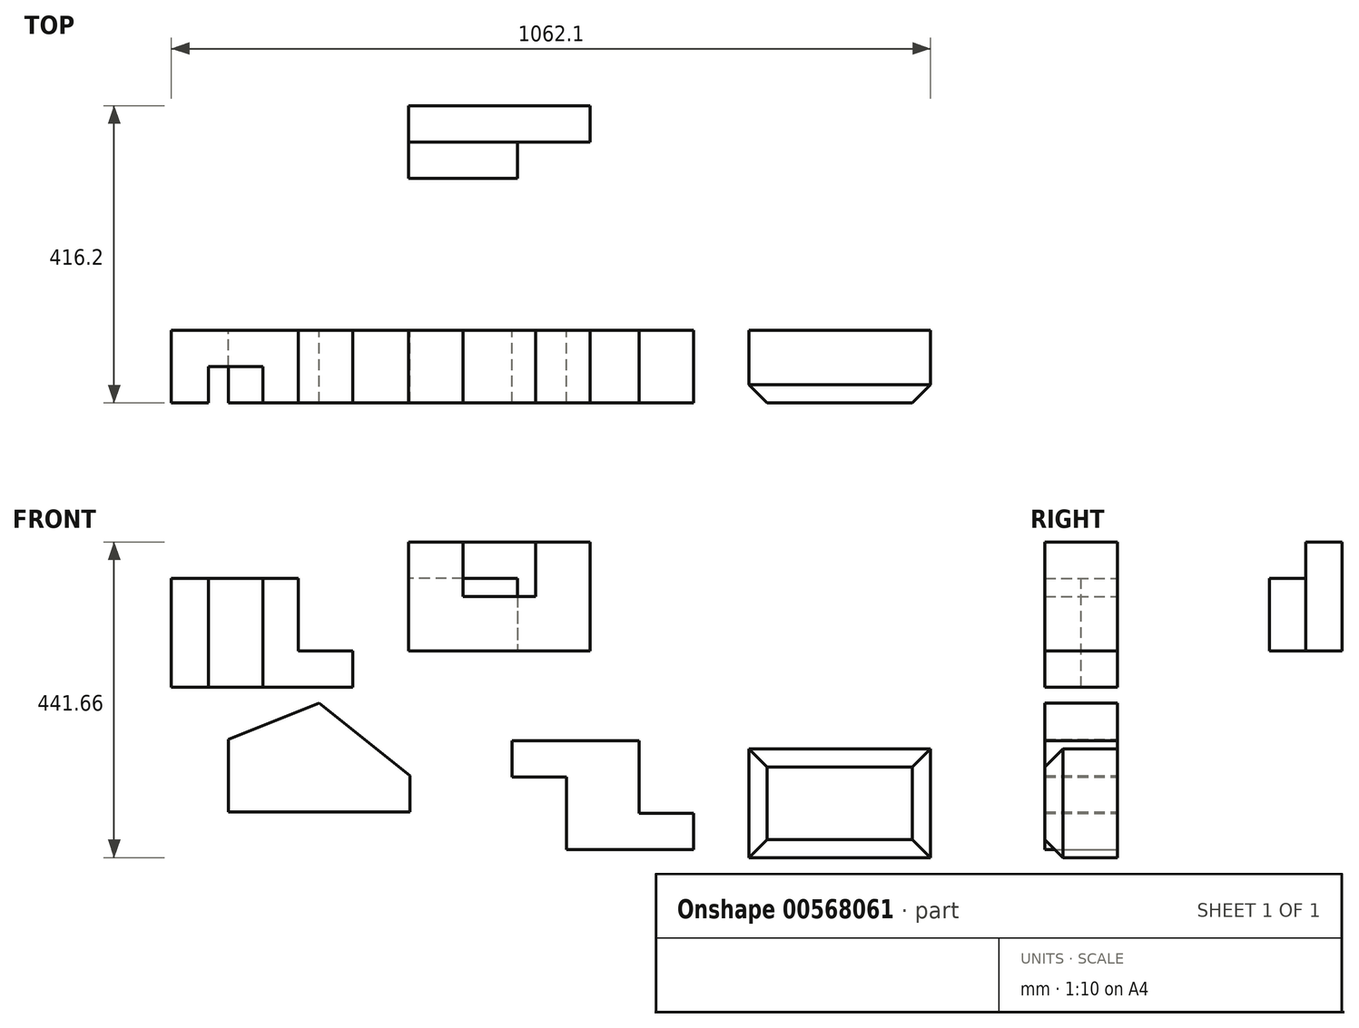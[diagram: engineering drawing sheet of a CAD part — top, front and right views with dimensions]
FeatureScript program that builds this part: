
annotation { "Feature Type Name" : "Feature", "Feature Type Description" : "" }
export const myFeature = defineFeature(function(context is Context, id is Id, definition is map)
    precondition{}
    {
        {
            var Q0;
            Q0=qCreatedBy(makeId("Front.planeOp"),FACE);
            var sketch = newSketch(context, id + "F0", { "sketchPlane" : qUnion([Q0])});
            skLineSegment(sketch, "E0", {"start": v(0, 0) * mm, "end": v(0, 152.4) * mm});
            skLineSegment(sketch, "E1", {"start": v(0, 152.4) * mm, "end": v(76.2, 152.4) * mm});
            skLineSegment(sketch, "E2", {"start": v(76.2, 152.4) * mm, "end": v(76.2, 76.2) * mm});
            skLineSegment(sketch, "E3", {"start": v(76.2, 76.2) * mm, "end": v(177.8, 76.2) * mm});
            skLineSegment(sketch, "E4", {"start": v(177.8, 76.2) * mm, "end": v(177.8, 152.4) * mm});
            skLineSegment(sketch, "E5", {"start": v(177.8, 152.4) * mm, "end": v(254, 152.4) * mm});
            skLineSegment(sketch, "E6", {"start": v(254, 152.4) * mm, "end": v(254, 0) * mm});
            skLineSegment(sketch, "E7", {"start": v(254, 0) * mm, "end": v(0, 0) * mm});
            skSolve(sketch);
        }
        {
            var Q0;
            Q0=makeQuery(id+"F0.imprint","IMPRINT",FACE,{"disambiguationData":[TD([[makeQuery(id+"F0.imprint","IMPRINT",EDGE,{"derivedFrom":sQuery(id+"F0.wireOp",EDGE,"E0")}),-1.0]])]});
            extrude(context, id + "F1", {"entities" : qUnion([Q0]), "depth" : 101.6 * mm, "offsetDistance" : 25.4 * mm});
        }
        {
            var Q0;
            Q0=qCreatedBy(makeId("Right.planeOp"),FACE);
            var sketch = newSketch(context, id + "F2", { "sketchPlane" : qUnion([Q0])});
            skLineSegment(sketch, "E8", {"start": v(213, 0) * mm, "end": v(314.6, 0) * mm});
            skLineSegment(sketch, "E9", {"start": v(314.6, 0) * mm, "end": v(314.6, 152.4) * mm});
            skLineSegment(sketch, "E10", {"start": v(314.6, 152.4) * mm, "end": v(263.8, 152.4) * mm});
            skLineSegment(sketch, "E11", {"start": v(263.8, 152.4) * mm, "end": v(263.8, 101.6) * mm});
            skLineSegment(sketch, "E12", {"start": v(263.8, 101.6) * mm, "end": v(213, 101.6) * mm});
            skLineSegment(sketch, "E13", {"start": v(213, 101.6) * mm, "end": v(213, 0) * mm});
            skSolve(sketch);
        }
        {
            var Q0;
            Q0=makeQuery(id+"F2.imprint","IMPRINT",FACE,{"disambiguationData":[TD([[makeQuery(id+"F2.imprint","IMPRINT",EDGE,{"derivedFrom":sQuery(id+"F2.wireOp",EDGE,"E8")}),1.0]])]});
            extrude(context, id + "F3", {"entities" : qUnion([Q0]), "depth" : 254 * mm, "offsetDistance" : 25.4 * mm});
        }
        {
            var Q0;
            Q0=makeQuery(id+"F3.opExtrude","CAP_FACE",FACE,{"disambiguationData":[OSD([sQuery(id+"F2.wireOp",EDGE,"E8"),sQuery(id+"F2.wireOp",EDGE,"E9"),sQuery(id+"F2.wireOp",EDGE,"E10"),sQuery(id+"F2.wireOp",EDGE,"E11"),sQuery(id+"F2.wireOp",EDGE,"E12"),sQuery(id+"F2.wireOp",EDGE,"E13")])],"isStart":false});
            var sketch = newSketch(context, id + "F4", { "sketchPlane" : qUnion([Q0])});
            skLineSegment(sketch, "E14", {"start": v(263.8, 101.6) * mm, "end": v(263.8, 0) * mm});
            skSolve(sketch);
        }
        {
            var Q0;
            {var subQ0=sQuery(id+"F4.wireOp",EDGE,"E14");Q0=makeQuery(id+"F4.imprint","IMPRINT",FACE,{"disambiguationData":[TD([[makeQuery(id+"F4.imprint","IMPRINT",EDGE,{"derivedFrom":subQ0}),-1.0]])]});}
            extrude(context, id + "F5", {"entities" : qUnion([Q0]), "operationType" : NewBodyOperationType.REMOVE, "oppositeDirection" : true, "depth" : 101.6 * mm, "offsetDistance" : 25.4 * mm});
        }
        {
            var Q0;
            Q0=qCreatedBy(makeId("Front.planeOp"),FACE);
            var sketch = newSketch(context, id + "F6", { "sketchPlane" : qUnion([Q0])});
            skLineSegment(sketch, "E15", {"start": v(-331.55, 101.6) * mm, "end": v(-331.55, -50.8) * mm});
            skLineSegment(sketch, "E16", {"start": v(-331.55, -50.8) * mm, "end": v(-77.55, -50.8) * mm});
            skLineSegment(sketch, "E17", {"start": v(-77.55, -50.8) * mm, "end": v(-77.55, 0) * mm});
            skLineSegment(sketch, "E18", {"start": v(-77.55, 0) * mm, "end": v(-153.75, 0) * mm});
            skLineSegment(sketch, "E19", {"start": v(-153.75, 0) * mm, "end": v(-153.75, 101.6) * mm});
            skLineSegment(sketch, "E20", {"start": v(-153.75, 101.6) * mm, "end": v(-331.55, 101.6) * mm});
            skLineSegment(sketch, "E21", {"start": v(-331.55, 101.6) * mm, "end": v(-280.75, 101.6) * mm});
            skSolve(sketch);
        }
        {
            var Q0;
            Q0=makeQuery(id+"F6.imprint","IMPRINT",FACE,{"disambiguationData":[TD([[makeQuery(id+"F6.imprint","IMPRINT",EDGE,{"derivedFrom":sQuery(id+"F6.wireOp",EDGE,"E15")}),1.0]])]});
            extrude(context, id + "F7", {"entities" : qUnion([Q0]), "depth" : 101.6 * mm, "offsetDistance" : 25.4 * mm});
        }
        {
            var Q0;
            Q0=makeQuery(id+"F7.opExtrude","SWEPT_FACE",FACE,{"disambiguationData":[OSD([sQuery(id+"F6.wireOp",EDGE,"E20"),sQuery(id+"F6.wireOp",EDGE,"E21")])]});
            var sketch = newSketch(context, id + "F8", { "sketchPlane" : qUnion([Q0])});
            skLineSegment(sketch, "E22", {"start": v(-331.55, -101.6) * mm, "end": v(-279.8, -101.6) * mm});
            skLineSegment(sketch, "E23", {"start": v(-279.8, -101.6) * mm, "end": v(-279.8, -50.8) * mm});
            skLineSegment(sketch, "E24", {"start": v(-279.8, -50.8) * mm, "end": v(-203.6, -50.8) * mm});
            skLineSegment(sketch, "E25", {"start": v(-203.6, -50.8) * mm, "end": v(-203.6, -101.6) * mm});
            skLineSegment(sketch, "E26", {"start": v(-203.6, -101.6) * mm, "end": v(-279.8, -101.6) * mm});
            skSolve(sketch);
        }
        {
            var Q0;
            Q0=makeQuery(id+"F8.imprint","IMPRINT",FACE,{"disambiguationData":[TD([[makeQuery(id+"F8.imprint","IMPRINT",EDGE,{"derivedFrom":sQuery(id+"F8.wireOp",EDGE,"E23")}),-1.0]])]});
            extrude(context, id + "F9", {"entities" : qUnion([Q0]), "operationType" : NewBodyOperationType.REMOVE, "oppositeDirection" : true, "depth" : 152.4 * mm, "offsetDistance" : 25.4 * mm});
        }
        {
            var Q0;
            Q0=qCreatedBy(makeId("Front.planeOp"),FACE);
            var sketch = newSketch(context, id + "F10", { "sketchPlane" : qUnion([Q0])});
            skLineSegment(sketch, "E27", {"start": v(144.83, -125.66) * mm, "end": v(144.83, -176.46) * mm});
            skLineSegment(sketch, "E28", {"start": v(144.83, -176.46) * mm, "end": v(221.03, -176.46) * mm});
            skLineSegment(sketch, "E29", {"start": v(221.03, -176.46) * mm, "end": v(221.03, -278.06) * mm});
            skLineSegment(sketch, "E30", {"start": v(221.03, -278.06) * mm, "end": v(398.83, -278.06) * mm});
            skLineSegment(sketch, "E31", {"start": v(398.83, -278.06) * mm, "end": v(398.83, -227.26) * mm});
            skLineSegment(sketch, "E32", {"start": v(398.83, -227.26) * mm, "end": v(322.63, -227.26) * mm});
            skLineSegment(sketch, "E33", {"start": v(322.63, -227.26) * mm, "end": v(322.63, -125.66) * mm});
            skLineSegment(sketch, "E34", {"start": v(322.63, -125.66) * mm, "end": v(144.83, -125.66) * mm});
            skSolve(sketch);
        }
        {
            var Q0;
            Q0=makeQuery(id+"F10.imprint","IMPRINT",FACE,{"disambiguationData":[TD([[makeQuery(id+"F10.imprint","IMPRINT",EDGE,{"derivedFrom":sQuery(id+"F10.wireOp",EDGE,"E27")}),1.0]])]});
            extrude(context, id + "F11", {"entities" : qUnion([Q0]), "depth" : 101.6 * mm, "offsetDistance" : 25.4 * mm});
        }
        {
            var Q0;
            Q0=qCreatedBy(makeId("Front.planeOp"),FACE);
            var sketch = newSketch(context, id + "F12", { "sketchPlane" : qUnion([Q0])});
            skLineSegment(sketch, "E35", {"start": v(-251.78, -124.08) * mm, "end": v(-251.78, -225.68) * mm});
            skLineSegment(sketch, "E36", {"start": v(-251.78, -225.68) * mm, "end": v(2.22, -225.68) * mm});
            skLineSegment(sketch, "E37", {"start": v(2.22, -225.68) * mm, "end": v(2.22, -174.88) * mm});
            skLineSegment(sketch, "E38", {"start": v(2.22, -174.88) * mm, "end": v(-124.78, -73.28) * mm});
            skLineSegment(sketch, "E39", {"start": v(-124.78, -73.28) * mm, "end": v(-251.78, -124.08) * mm});
            skSolve(sketch);
        }
        {
            var Q0;
            Q0=makeQuery(id+"F12.imprint","IMPRINT",FACE,{"disambiguationData":[TD([[makeQuery(id+"F12.imprint","IMPRINT",EDGE,{"derivedFrom":sQuery(id+"F12.wireOp",EDGE,"E35")}),1.0]])]});
            extrude(context, id + "F13", {"entities" : qUnion([Q0]), "depth" : 101.6 * mm, "offsetDistance" : 25.4 * mm});
        }
        {
            var Q0;
            Q0=qCreatedBy(makeId("Front.planeOp"),FACE);
            var sketch = newSketch(context, id + "F14", { "sketchPlane" : qUnion([Q0])});
            skLineSegment(sketch, "E40", {"start": v(476.55, -136.86) * mm, "end": v(476.55, -289.26) * mm});
            skLineSegment(sketch, "E41", {"start": v(476.55, -289.26) * mm, "end": v(730.55, -289.26) * mm});
            skLineSegment(sketch, "E42", {"start": v(730.55, -289.26) * mm, "end": v(730.55, -136.86) * mm});
            skLineSegment(sketch, "E43", {"start": v(730.55, -136.86) * mm, "end": v(476.55, -136.86) * mm});
            skSolve(sketch);
        }
        {
            var Q0;
            Q0=makeQuery(id+"F14.imprint","IMPRINT",FACE,{"disambiguationData":[TD([[makeQuery(id+"F14.imprint","IMPRINT",EDGE,{"derivedFrom":sQuery(id+"F14.wireOp",EDGE,"E40")}),1.0]])]});
            extrude(context, id + "F15", {"entities" : qUnion([Q0]), "depth" : 101.6 * mm, "offsetDistance" : 25.4 * mm});
        }
        {
            var Q0;
            Q0=makeQuery(id+"F15.opExtrude","CAP_FACE",FACE,{"disambiguationData":[OSD([sQuery(id+"F14.wireOp",EDGE,"E40"),sQuery(id+"F14.wireOp",EDGE,"E41"),sQuery(id+"F14.wireOp",EDGE,"E42"),sQuery(id+"F14.wireOp",EDGE,"E43")])],"isStart":false});
            chamfer(context, id + "F16", {"entities" : qUnion([Q0]), "width" : 25.4 * mm, "tangentPropagation" : true});
        }
    });
